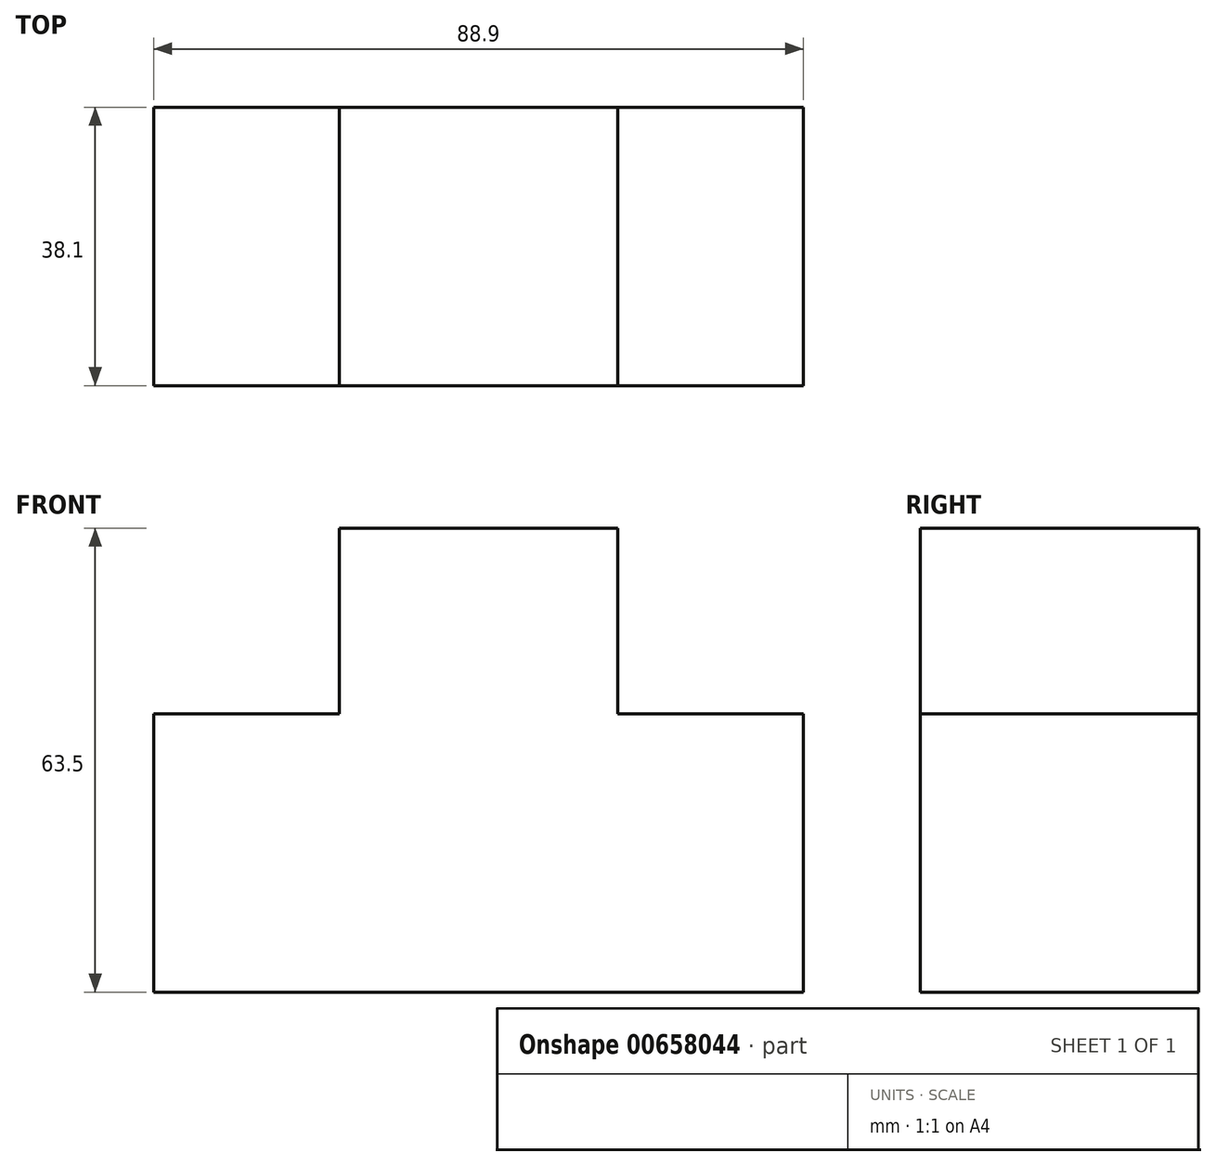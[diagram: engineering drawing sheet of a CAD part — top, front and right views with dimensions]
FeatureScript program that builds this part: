
annotation { "Feature Type Name" : "Feature", "Feature Type Description" : "" }
export const myFeature = defineFeature(function(context is Context, id is Id, definition is map)
    precondition{}
    {
        {
            var Q0;
            Q0=qCreatedBy(makeId("Front.planeOp"),FACE);
            var sketch = newSketch(context, id + "F0", { "sketchPlane" : qUnion([Q0])});
            skLineSegment(sketch, "E0", {"start": v(-41.4, -23.1) * mm, "end": v(47.5, -23.1) * mm});
            skLineSegment(sketch, "E1", {"start": v(47.5, -23.1) * mm, "end": v(47.5, 15) * mm});
            skLineSegment(sketch, "E2", {"start": v(47.5, 15) * mm, "end": v(22.1, 15) * mm});
            skLineSegment(sketch, "E3", {"start": v(22.1, 15) * mm, "end": v(22.1, 40.4) * mm});
            skLineSegment(sketch, "E4", {"start": v(22.1, 40.4) * mm, "end": v(-16, 40.4) * mm});
            skLineSegment(sketch, "E5", {"start": v(-16, 40.4) * mm, "end": v(-16, 15) * mm});
            skLineSegment(sketch, "E6", {"start": v(-16, 15) * mm, "end": v(-41.4, 15) * mm});
            skLineSegment(sketch, "E7", {"start": v(-41.4, 15) * mm, "end": v(-41.4, -23.1) * mm});
            skSolve(sketch);
        }
        {
            var Q0;
            Q0=makeQuery(id+"F0.imprint","IMPRINT",FACE,{"disambiguationData":[TD([[makeQuery(id+"F0.imprint","IMPRINT",EDGE,{"derivedFrom":sQuery(id+"F0.wireOp",EDGE,"E0")}),1.0]])]});
            extrude(context, id + "F1", {"entities" : qUnion([Q0]), "depth" : 38.1 * mm, "offsetDistance" : 25.4 * mm});
        }
    });
